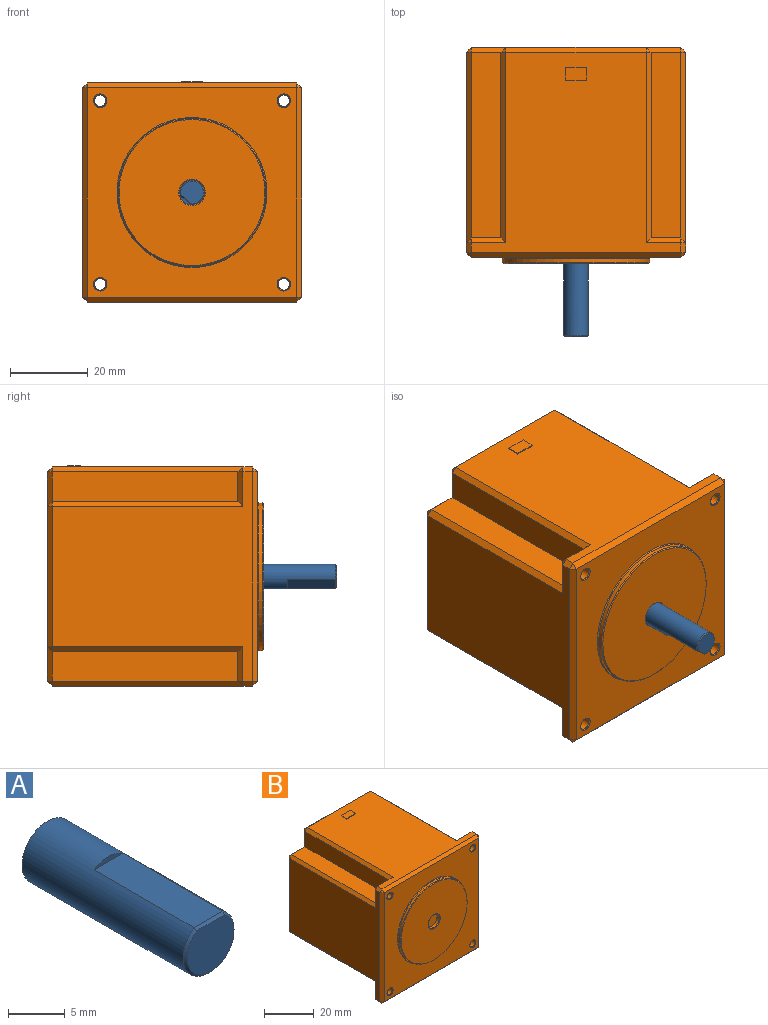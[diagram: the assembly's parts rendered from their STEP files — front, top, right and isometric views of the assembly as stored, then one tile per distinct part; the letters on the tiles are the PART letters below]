
ASSEMBLY  parts=2 mates=1
PART A: 7 faces, bbox 6.4x20.3x6.4 mm
  f0: cylinder r=3.17mm len=20.07mm, axis (0,1,0), area 352.7mm2, adj f2,f3,f4,f5
  f1: plane 5.84x5.28mm, normal (0,-1,0), area 25.5mm2, adj f5,f6
  f2: plane 6.35x6.35mm, normal (0,1,0), area 31.7mm2, adj f0
  f3: plane 12.45x3.6mm, normal (0,0,1), area 44.8mm2, adj f0,f4,f6
  f4: plane 3.6x0.56mm, normal (0,-1,0), area 1.4mm2, adj f0,f3
  f5: cone r=2.92mm half-angle=45deg, axis (0,1,0), area 5.5mm2, adj f0,f1,f6
  f6: plane 3.6x0.26mm, normal (0,-0.71,0.71), area 1.3mm2, adj f1,f3,f5
PART B: 94 faces, bbox 56.4x55.6x56.6 mm
  f0: plane 53.85x51.56mm, normal (0,0,1), area 1887.9mm2, adj f27,f28,f31,f36,f41,f42,f43,f44
  f1: plane 53.85x51.56mm, normal (0,0,-1), area 1904.9mm2, adj f48,f49,f59,f60,f64,f69,f72,f73
  f2: plane 53.85x51.56mm, normal (1,0,0), area 1904.9mm2, adj f41,f50,f56,f60,f61,f66,f70,f71
  f3: plane 53.85x51.56mm, normal (-1,0,0), area 1904.9mm2, adj f27,f29,f34,f35,f45,f46,f47,f48
  f4: plane 53.85x53.85mm, normal (0,1,0), area 2583.5mm2, adj f32,f33,f44,f45,f57,f58,f62,f63
  f5: cylinder r=1.49mm len=4.57mm, axis (0,-1,0), area 42.7mm2, adj f82,f88
  f6: cylinder r=1.49mm len=4.57mm, axis (0,-1,0), area 42.7mm2, adj f83,f86
  f7: cylinder r=1.49mm len=4.57mm, axis (0,-1,0), area 42.7mm2, adj f84,f85
  f8: cylinder r=1.49mm len=4.57mm, axis (0,-1,0), area 42.7mm2, adj f81,f87
  f9: plane 53.85x53.85mm, normal (0,-1,0), area 1690.9mm2, adj f35,f36,f49,f50,f80,f81,f82,f83
  f10: cylinder r=3.17mm len=6.35mm, axis (0,1,0), area 25.3mm2, adj f13,f78
  f11: cylinder r=19.05mm len=38.1mm, axis (0,1,0), area 121.6mm2, adj f79,f80
  f12: plane 37.59x37.59mm, normal (0,-1,0), area 1073mm2, adj f78,f79
  f13: plane 6.35x6.35mm, normal (0,-1,0), area 31.7mm2, adj f10
  f14: plane 7.62x7.62mm, normal (0,1,0), area 48.6mm2, adj f15,f16,f47,f59,f87
  f15: plane 47.75x7.62mm, normal (-1,0,0), area 363.9mm2, adj f14,f16,f63,f64
  f16: plane 47.75x7.62mm, normal (0,0,-1), area 363.9mm2, adj f14,f15,f46,f58
  f17: plane 7.62x7.62mm, normal (0,1,0), area 48.6mm2, adj f18,f19,f66,f69,f85
  f18: plane 47.75x7.62mm, normal (1,0,0), area 363.9mm2, adj f17,f19,f73,f77
  f19: plane 47.75x7.62mm, normal (0,0,-1), area 363.9mm2, adj f17,f18,f70,f76
  f20: plane 7.62x7.62mm, normal (0,1,0), area 48.6mm2, adj f21,f22,f42,f56,f86
  f21: plane 47.75x7.62mm, normal (1,0,0), area 363.9mm2, adj f20,f22,f43,f57
  f22: plane 47.75x7.62mm, normal (0,0,1), area 363.9mm2, adj f20,f21,f61,f62
  f23: plane 7.62x7.62mm, normal (0,1,0), area 48.6mm2, adj f24,f25,f28,f29,f88
  f24: plane 47.75x7.62mm, normal (-1,0,0), area 363.9mm2, adj f23,f25,f31,f32
  f25: plane 47.75x7.62mm, normal (0,0,1), area 363.9mm2, adj f23,f24,f33,f34
  f26: plane 1.27x1.27mm, normal (-0.58,0.58,0.58), area 1.4mm2, adj f27,f28,f29
  f27: plane 2.54x1.27mm, normal (-0.71,0,0.71), area 4.6mm2, adj f0,f3,f26,f30
  f28: plane 8.89x1.27mm, normal (0,0.71,0.71), area 14.8mm2, adj f0,f23,f26,f31
  f29: plane 8.89x1.27mm, normal (-0.71,0.71,0), area 14.8mm2, adj f3,f23,f26,f34
  f30: plane 1.27x1.27mm, normal (-0.58,-0.58,0.58), area 1.4mm2, adj f27,f35,f36
  f31: plane 49.02x1.27mm, normal (-0.71,0,0.71), area 86.9mm2, adj f0,f24,f28,f37
  f32: plane 8.89x1.27mm, normal (-0.71,0.71,0), area 14.8mm2, adj f4,f24,f33,f37
  f33: plane 8.89x1.27mm, normal (0,0.71,0.71), area 14.8mm2, adj f4,f25,f32,f38
  f34: plane 49.02x1.27mm, normal (-0.71,0,0.71), area 86.9mm2, adj f3,f25,f29,f38
  f35: plane 53.85x1.27mm, normal (-0.71,-0.71,0), area 96.7mm2, adj f3,f9,f30,f39
  f36: plane 53.85x1.27mm, normal (0,-0.71,0.71), area 96.7mm2, adj f0,f9,f30,f40
  f37: plane 1.27x1.27mm, normal (-0.58,0.58,0.58), area 1.4mm2, adj f31,f32,f44
  f38: plane 1.27x1.27mm, normal (-0.58,0.58,0.58), area 1.4mm2, adj f33,f34,f45
  f39: plane 1.27x1.27mm, normal (-0.58,-0.58,-0.58), area 1.4mm2, adj f35,f48,f49
  f40: plane 1.27x1.27mm, normal (0.58,-0.58,0.58), area 1.4mm2, adj f36,f41,f50
  f41: plane 2.54x1.27mm, normal (0.71,0,0.71), area 4.6mm2, adj f0,f2,f40,f51
  f42: plane 8.89x1.27mm, normal (0,0.71,0.71), area 14.8mm2, adj f0,f20,f43,f51
  f43: plane 49.02x1.27mm, normal (0.71,0,0.71), area 86.9mm2, adj f0,f21,f42,f52
  f44: plane 36.07x1.27mm, normal (0,0.71,0.71), area 64.8mm2, adj f0,f4,f37,f52
  f45: plane 36.07x1.27mm, normal (-0.71,0.71,0), area 64.8mm2, adj f3,f4,f38,f53
  f46: plane 49.02x1.27mm, normal (-0.71,0,-0.71), area 86.9mm2, adj f3,f16,f47,f53
  f47: plane 8.89x1.27mm, normal (-0.71,0.71,0), area 14.8mm2, adj f3,f14,f46,f54
  f48: plane 2.54x1.27mm, normal (-0.71,0,-0.71), area 4.6mm2, adj f1,f3,f39,f54
  f49: plane 53.85x1.27mm, normal (0,-0.71,-0.71), area 96.7mm2, adj f1,f9,f39,f55
  f50: plane 53.85x1.27mm, normal (0.71,-0.71,0), area 96.7mm2, adj f2,f9,f40,f55
  f51: plane 1.27x1.27mm, normal (0.58,0.58,0.58), area 1.4mm2, adj f41,f42,f56
  f52: plane 1.27x1.27mm, normal (0.58,0.58,0.58), area 1.4mm2, adj f43,f44,f57
  f53: plane 1.27x1.27mm, normal (-0.58,0.58,-0.58), area 1.4mm2, adj f45,f46,f58
  f54: plane 1.27x1.27mm, normal (-0.58,0.58,-0.58), area 1.4mm2, adj f47,f48,f59
  f55: plane 1.27x1.27mm, normal (0.58,-0.58,-0.58), area 1.4mm2, adj f49,f50,f60
  f56: plane 8.89x1.27mm, normal (0.71,0.71,0), area 14.8mm2, adj f2,f20,f51,f61
  f57: plane 8.89x1.27mm, normal (0.71,0.71,0), area 14.8mm2, adj f4,f21,f52,f62
  f58: plane 8.89x1.27mm, normal (0,0.71,-0.71), area 14.8mm2, adj f4,f16,f53,f63
  f59: plane 8.89x1.27mm, normal (0,0.71,-0.71), area 14.8mm2, adj f1,f14,f54,f64
  f60: plane 2.54x1.27mm, normal (0.71,0,-0.71), area 4.6mm2, adj f1,f2,f55,f65
  f61: plane 49.02x1.27mm, normal (0.71,0,0.71), area 86.9mm2, adj f2,f22,f56,f67
  f62: plane 8.89x1.27mm, normal (0,0.71,0.71), area 14.8mm2, adj f4,f22,f57,f67
  f63: plane 8.89x1.27mm, normal (-0.71,0.71,0), area 14.8mm2, adj f4,f15,f58,f68
  f64: plane 49.02x1.27mm, normal (-0.71,0,-0.71), area 86.9mm2, adj f1,f15,f59,f68
  f65: plane 1.27x1.27mm, normal (0.58,0.58,-0.58), area 1.4mm2, adj f60,f66,f69
  f66: plane 8.89x1.27mm, normal (0.71,0.71,0), area 14.8mm2, adj f2,f17,f65,f70
  f67: plane 1.27x1.27mm, normal (0.58,0.58,0.58), area 1.4mm2, adj f61,f62,f71
  f68: plane 1.27x1.27mm, normal (-0.58,0.58,-0.58), area 1.4mm2, adj f63,f64,f72
  f69: plane 8.89x1.27mm, normal (0,0.71,-0.71), area 14.8mm2, adj f1,f17,f65,f73
  f70: plane 49.02x1.27mm, normal (0.71,0,-0.71), area 86.9mm2, adj f2,f19,f66,f74
  f71: plane 36.07x1.27mm, normal (0.71,0.71,0), area 64.8mm2, adj f2,f4,f67,f74
  f72: plane 36.07x1.27mm, normal (0,0.71,-0.71), area 64.8mm2, adj f1,f4,f68,f75
  f73: plane 49.02x1.27mm, normal (0.71,0,-0.71), area 86.9mm2, adj f1,f18,f69,f75
  f74: plane 1.27x1.27mm, normal (0.58,0.58,-0.58), area 1.4mm2, adj f70,f71,f76
  f75: plane 1.27x1.27mm, normal (0.58,0.58,-0.58), area 1.4mm2, adj f72,f73,f77
  f76: plane 8.89x1.27mm, normal (0,0.71,-0.71), area 14.8mm2, adj f4,f19,f74,f77
  f77: plane 8.89x1.27mm, normal (0.71,0.71,0), area 14.8mm2, adj f4,f18,f75,f76
  f78: cone r=3.17mm half-angle=45deg, axis (0,-1,0), area 7.5mm2, adj f10,f12
  f79: cone r=18.8mm half-angle=45deg, axis (0,1,0), area 42.7mm2, adj f11,f12
  f80: cone r=19.05mm half-angle=45deg, axis (0,1,0), area 43.3mm2, adj f9,f11
  f81: cone r=1.49mm half-angle=45deg, axis (0,-1,0), area 3.6mm2, adj f8,f9
  f82: cone r=1.49mm half-angle=45deg, axis (0,-1,0), area 3.6mm2, adj f5,f9
  f83: cone r=1.49mm half-angle=45deg, axis (0,-1,0), area 3.6mm2, adj f6,f9
  f84: cone r=1.49mm half-angle=45deg, axis (0,-1,0), area 3.6mm2, adj f7,f9
  f85: cone r=1.74mm half-angle=45deg, axis (0,1,0), area 3.6mm2, adj f7,f17
  f86: cone r=1.74mm half-angle=45deg, axis (0,1,0), area 3.6mm2, adj f6,f20
  f87: cone r=1.74mm half-angle=45deg, axis (0,1,0), area 3.6mm2, adj f8,f14
  f88: cone r=1.74mm half-angle=45deg, axis (0,1,0), area 3.6mm2, adj f5,f23
  f89: plane 5.22x0.25mm, normal (0,-1,0), area 1.3mm2, adj f0,f90,f92,f93
  f90: plane 3.27x0.25mm, normal (1,0,0), area 0.8mm2, adj f0,f89,f91,f93
  f91: plane 5.22x0.25mm, normal (0,1,0), area 1.3mm2, adj f0,f90,f92,f93
  f92: plane 3.27x0.25mm, normal (-1,0,0), area 0.8mm2, adj f0,f89,f91,f93
  f93: plane 5.22x3.27mm, normal (0,0,1), area 17mm2, adj f89,f90,f91,f92
PLACE A rot(axis=(0,-1,0),136.9deg) t=(0,0,0)mm
PLACE B at identity
MATE cylindrical A.f0 <-> B.f10  axis (0,-1,0) through (0,0,0)mm
